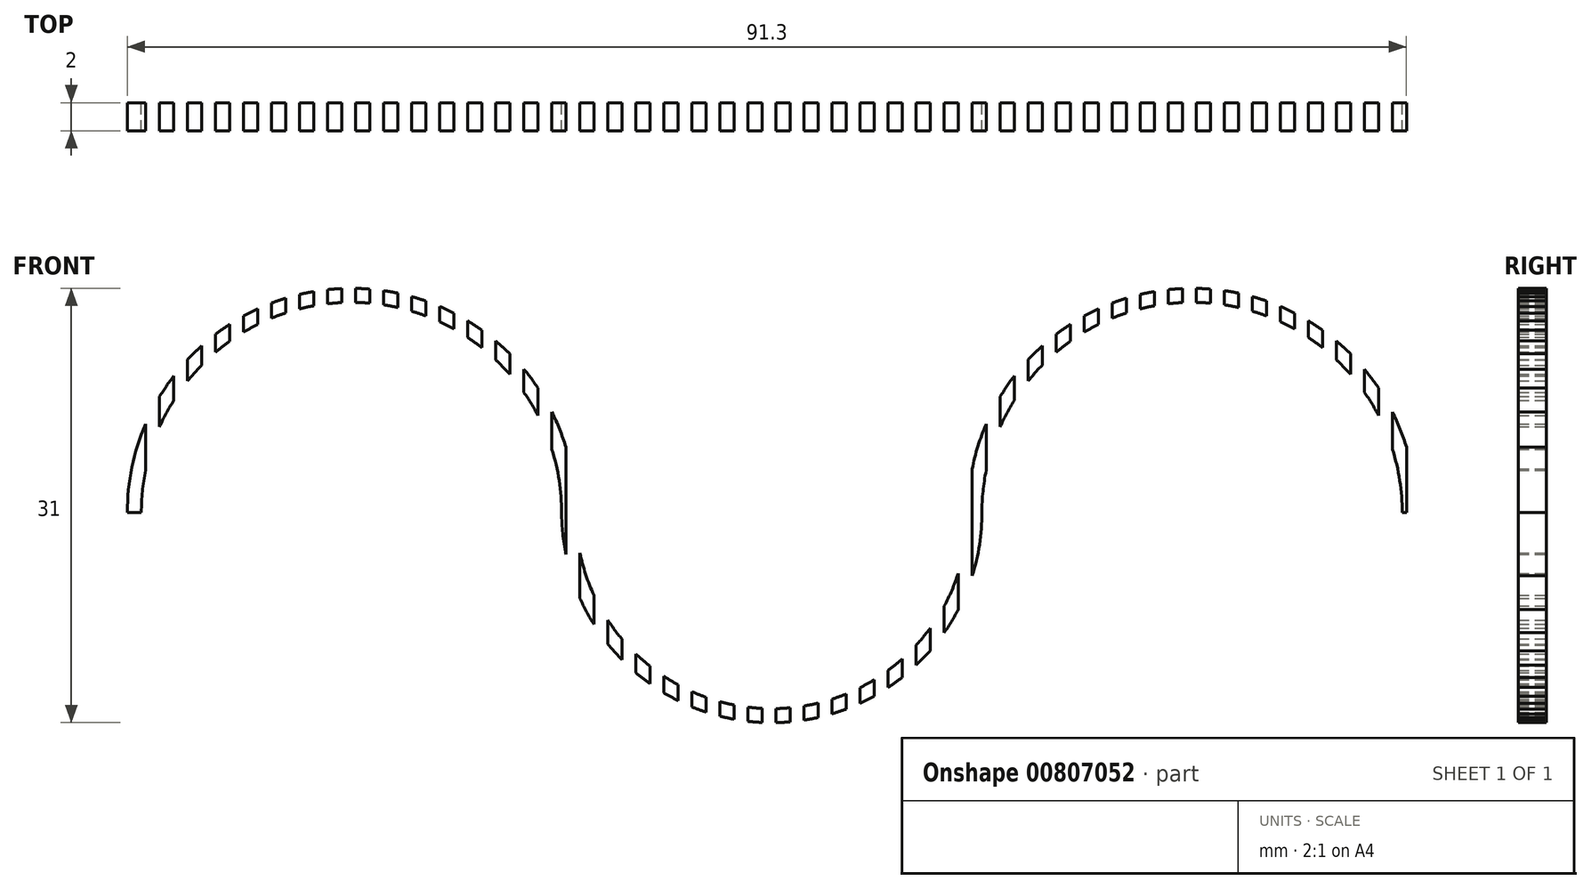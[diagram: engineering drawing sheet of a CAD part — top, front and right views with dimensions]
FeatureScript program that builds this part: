
annotation { "Feature Type Name" : "Feature", "Feature Type Description" : "" }
export const myFeature = defineFeature(function(context is Context, id is Id, definition is map)
    precondition{}
    {
        {
            var Q0;
            Q0=qCreatedBy(makeId("Front.planeOp"),FACE);
            var sketch = newSketch(context, id + "F0", { "sketchPlane" : qUnion([Q0])});
            skArc(sketch, "E0", {"start": v(-15, 0) * mm, "mid": v(0, 15) * mm, "end": v(15, 0) * mm});
            skArc(sketch, "E1", {"start": v(-45, 0) * mm, "mid": v(-30, -15) * mm, "end": v(-15, 0) * mm});
            skLineSegment(sketch, "E2", {"start": v(-15, 0) * mm, "end": v(-84.52, 0) * mm, "construction": true});
            skArc(sketch, "E3", {"start": v(-45, 0) * mm, "mid": v(-60, 15) * mm, "end": v(-75, 0) * mm});
            skArc(sketch, "E4.0", {"start": v(-44, 0) * mm, "mid": v(-60, 16) * mm, "end": v(-76, 0) * mm});
            skArc(sketch, "E4.1", {"start": v(-44, 0) * mm, "mid": v(-30, -14) * mm, "end": v(-16, 0) * mm});
            skArc(sketch, "E4.2", {"start": v(-16, 0) * mm, "mid": v(0, 16) * mm, "end": v(16, 0) * mm});
            skLineSegment(sketch, "E5", {"start": v(-76, 0) * mm, "end": v(-75, 0) * mm});
            skLineSegment(sketch, "E6", {"start": v(15, 0) * mm, "end": v(16, 0) * mm});
            skSolve(sketch);
        }
        {
            var Q0;
            Q0 = qSketchRegion(id + "F0", true);
            extrude(context, id + "F1", {"entities" : qUnion([Q0]), "depth" : 2 * mm, "offsetDistance" : 25 * mm});
        }
        {
            var Q0;
            Q0=qCreatedBy(makeId("Front.planeOp"),FACE);
            var sketch = newSketch(context, id + "F2", { "sketchPlane" : qUnion([Q0])});
            skLineSegment(sketch, "E7.bottom", {"start": v(-74.7, 18.01) * mm, "end": v(-73.7, 18.01) * mm});
            skLineSegment(sketch, "E7.top", {"start": v(-74.7, -16.05) * mm, "end": v(-73.7, -16.05) * mm});
            skLineSegment(sketch, "E7.left", {"start": v(-74.7, 18.01) * mm, "end": v(-74.7, -16.05) * mm});
            skLineSegment(sketch, "E7.right", {"start": v(-73.7, 18.01) * mm, "end": v(-73.7, -16.05) * mm});
            skLineSegment(sketch, "E8.1.0.0", {"start": v(-71.7, 18.01) * mm, "end": v(-71.7, -16.05) * mm});
            skLineSegment(sketch, "E8.1.0.1", {"start": v(-72.7, 18.01) * mm, "end": v(-72.7, -16.05) * mm});
            skLineSegment(sketch, "E8.1.0.2", {"start": v(-72.7, -16.05) * mm, "end": v(-71.7, -16.05) * mm});
            skLineSegment(sketch, "E8.1.0.3", {"start": v(-72.7, 18.01) * mm, "end": v(-71.7, 18.01) * mm});
            skLineSegment(sketch, "E8.2.0.0", {"start": v(-69.7, 18.01) * mm, "end": v(-69.7, -16.05) * mm});
            skLineSegment(sketch, "E8.2.0.1", {"start": v(-70.7, 18.01) * mm, "end": v(-70.7, -16.05) * mm});
            skLineSegment(sketch, "E8.2.0.2", {"start": v(-70.7, -16.05) * mm, "end": v(-69.7, -16.05) * mm});
            skLineSegment(sketch, "E8.2.0.3", {"start": v(-70.7, 18.01) * mm, "end": v(-69.7, 18.01) * mm});
            skLineSegment(sketch, "E8.3.0.0", {"start": v(-67.7, 18.01) * mm, "end": v(-67.7, -16.05) * mm});
            skLineSegment(sketch, "E8.3.0.1", {"start": v(-68.7, 18.01) * mm, "end": v(-68.7, -16.05) * mm});
            skLineSegment(sketch, "E8.3.0.2", {"start": v(-68.7, -16.05) * mm, "end": v(-67.7, -16.05) * mm});
            skLineSegment(sketch, "E8.3.0.3", {"start": v(-68.7, 18.01) * mm, "end": v(-67.7, 18.01) * mm});
            skLineSegment(sketch, "E8.4.0.0", {"start": v(-65.7, 18.01) * mm, "end": v(-65.7, -16.05) * mm});
            skLineSegment(sketch, "E8.4.0.1", {"start": v(-66.7, 18.01) * mm, "end": v(-66.7, -16.05) * mm});
            skLineSegment(sketch, "E8.4.0.2", {"start": v(-66.7, -16.05) * mm, "end": v(-65.7, -16.05) * mm});
            skLineSegment(sketch, "E8.4.0.3", {"start": v(-66.7, 18.01) * mm, "end": v(-65.7, 18.01) * mm});
            skLineSegment(sketch, "E8.5.0.0", {"start": v(-63.7, 18.01) * mm, "end": v(-63.7, -16.05) * mm});
            skLineSegment(sketch, "E8.5.0.1", {"start": v(-64.7, 18.01) * mm, "end": v(-64.7, -16.05) * mm});
            skLineSegment(sketch, "E8.5.0.2", {"start": v(-64.7, -16.05) * mm, "end": v(-63.7, -16.05) * mm});
            skLineSegment(sketch, "E8.5.0.3", {"start": v(-64.7, 18.01) * mm, "end": v(-63.7, 18.01) * mm});
            skLineSegment(sketch, "E8.6.0.0", {"start": v(-61.7, 18.01) * mm, "end": v(-61.7, -16.05) * mm});
            skLineSegment(sketch, "E8.6.0.1", {"start": v(-62.7, 18.01) * mm, "end": v(-62.7, -16.05) * mm});
            skLineSegment(sketch, "E8.6.0.2", {"start": v(-62.7, -16.05) * mm, "end": v(-61.7, -16.05) * mm});
            skLineSegment(sketch, "E8.6.0.3", {"start": v(-62.7, 18.01) * mm, "end": v(-61.7, 18.01) * mm});
            skLineSegment(sketch, "E8.7.0.0", {"start": v(-59.7, 18.01) * mm, "end": v(-59.7, -16.05) * mm});
            skLineSegment(sketch, "E8.7.0.1", {"start": v(-60.7, 18.01) * mm, "end": v(-60.7, -16.05) * mm});
            skLineSegment(sketch, "E8.7.0.2", {"start": v(-60.7, -16.05) * mm, "end": v(-59.7, -16.05) * mm});
            skLineSegment(sketch, "E8.7.0.3", {"start": v(-60.7, 18.01) * mm, "end": v(-59.7, 18.01) * mm});
            skLineSegment(sketch, "E8.8.0.0", {"start": v(-57.7, 18.01) * mm, "end": v(-57.7, -16.05) * mm});
            skLineSegment(sketch, "E8.8.0.1", {"start": v(-58.7, 18.01) * mm, "end": v(-58.7, -16.05) * mm});
            skLineSegment(sketch, "E8.8.0.2", {"start": v(-58.7, -16.05) * mm, "end": v(-57.7, -16.05) * mm});
            skLineSegment(sketch, "E8.8.0.3", {"start": v(-58.7, 18.01) * mm, "end": v(-57.7, 18.01) * mm});
            skLineSegment(sketch, "E8.9.0.0", {"start": v(-55.7, 18.01) * mm, "end": v(-55.7, -16.05) * mm});
            skLineSegment(sketch, "E8.9.0.1", {"start": v(-56.7, 18.01) * mm, "end": v(-56.7, -16.05) * mm});
            skLineSegment(sketch, "E8.9.0.2", {"start": v(-56.7, -16.05) * mm, "end": v(-55.7, -16.05) * mm});
            skLineSegment(sketch, "E8.9.0.3", {"start": v(-56.7, 18.01) * mm, "end": v(-55.7, 18.01) * mm});
            skLineSegment(sketch, "E8.10.0.0", {"start": v(-53.7, 18.01) * mm, "end": v(-53.7, -16.05) * mm});
            skLineSegment(sketch, "E8.10.0.1", {"start": v(-54.7, 18.01) * mm, "end": v(-54.7, -16.05) * mm});
            skLineSegment(sketch, "E8.10.0.2", {"start": v(-54.7, -16.05) * mm, "end": v(-53.7, -16.05) * mm});
            skLineSegment(sketch, "E8.10.0.3", {"start": v(-54.7, 18.01) * mm, "end": v(-53.7, 18.01) * mm});
            skLineSegment(sketch, "E8.11.0.0", {"start": v(-51.7, 18.01) * mm, "end": v(-51.7, -16.05) * mm});
            skLineSegment(sketch, "E8.11.0.1", {"start": v(-52.7, 18.01) * mm, "end": v(-52.7, -16.05) * mm});
            skLineSegment(sketch, "E8.11.0.2", {"start": v(-52.7, -16.05) * mm, "end": v(-51.7, -16.05) * mm});
            skLineSegment(sketch, "E8.11.0.3", {"start": v(-52.7, 18.01) * mm, "end": v(-51.7, 18.01) * mm});
            skLineSegment(sketch, "E8.12.0.0", {"start": v(-49.7, 18.01) * mm, "end": v(-49.7, -16.05) * mm});
            skLineSegment(sketch, "E8.12.0.1", {"start": v(-50.7, 18.01) * mm, "end": v(-50.7, -16.05) * mm});
            skLineSegment(sketch, "E8.12.0.2", {"start": v(-50.7, -16.05) * mm, "end": v(-49.7, -16.05) * mm});
            skLineSegment(sketch, "E8.12.0.3", {"start": v(-50.7, 18.01) * mm, "end": v(-49.7, 18.01) * mm});
            skLineSegment(sketch, "E8.13.0.0", {"start": v(-47.7, 18.01) * mm, "end": v(-47.7, -16.05) * mm});
            skLineSegment(sketch, "E8.13.0.1", {"start": v(-48.7, 18.01) * mm, "end": v(-48.7, -16.05) * mm});
            skLineSegment(sketch, "E8.13.0.2", {"start": v(-48.7, -16.05) * mm, "end": v(-47.7, -16.05) * mm});
            skLineSegment(sketch, "E8.13.0.3", {"start": v(-48.7, 18.01) * mm, "end": v(-47.7, 18.01) * mm});
            skLineSegment(sketch, "E8.14.0.0", {"start": v(-45.7, 18.01) * mm, "end": v(-45.7, -16.05) * mm});
            skLineSegment(sketch, "E8.14.0.1", {"start": v(-46.7, 18.01) * mm, "end": v(-46.7, -16.05) * mm});
            skLineSegment(sketch, "E8.14.0.2", {"start": v(-46.7, -16.05) * mm, "end": v(-45.7, -16.05) * mm});
            skLineSegment(sketch, "E8.14.0.3", {"start": v(-46.7, 18.01) * mm, "end": v(-45.7, 18.01) * mm});
            skLineSegment(sketch, "E8.15.0.0", {"start": v(-43.7, 18.01) * mm, "end": v(-43.7, -16.05) * mm});
            skLineSegment(sketch, "E8.15.0.1", {"start": v(-44.7, 18.01) * mm, "end": v(-44.7, -16.05) * mm});
            skLineSegment(sketch, "E8.15.0.2", {"start": v(-44.7, -16.05) * mm, "end": v(-43.7, -16.05) * mm});
            skLineSegment(sketch, "E8.15.0.3", {"start": v(-44.7, 18.01) * mm, "end": v(-43.7, 18.01) * mm});
            skLineSegment(sketch, "E8.16.0.0", {"start": v(-41.7, 18.01) * mm, "end": v(-41.7, -16.05) * mm});
            skLineSegment(sketch, "E8.16.0.1", {"start": v(-42.7, 18.01) * mm, "end": v(-42.7, -16.05) * mm});
            skLineSegment(sketch, "E8.16.0.2", {"start": v(-42.7, -16.05) * mm, "end": v(-41.7, -16.05) * mm});
            skLineSegment(sketch, "E8.16.0.3", {"start": v(-42.7, 18.01) * mm, "end": v(-41.7, 18.01) * mm});
            skLineSegment(sketch, "E8.17.0.0", {"start": v(-39.7, 18.01) * mm, "end": v(-39.7, -16.05) * mm});
            skLineSegment(sketch, "E8.17.0.1", {"start": v(-40.7, 18.01) * mm, "end": v(-40.7, -16.05) * mm});
            skLineSegment(sketch, "E8.17.0.2", {"start": v(-40.7, -16.05) * mm, "end": v(-39.7, -16.05) * mm});
            skLineSegment(sketch, "E8.17.0.3", {"start": v(-40.7, 18.01) * mm, "end": v(-39.7, 18.01) * mm});
            skLineSegment(sketch, "E8.18.0.0", {"start": v(-37.7, 18.01) * mm, "end": v(-37.7, -16.05) * mm});
            skLineSegment(sketch, "E8.18.0.1", {"start": v(-38.7, 18.01) * mm, "end": v(-38.7, -16.05) * mm});
            skLineSegment(sketch, "E8.18.0.2", {"start": v(-38.7, -16.05) * mm, "end": v(-37.7, -16.05) * mm});
            skLineSegment(sketch, "E8.18.0.3", {"start": v(-38.7, 18.01) * mm, "end": v(-37.7, 18.01) * mm});
            skLineSegment(sketch, "E8.19.0.0", {"start": v(-35.7, 18.01) * mm, "end": v(-35.7, -16.05) * mm});
            skLineSegment(sketch, "E8.19.0.1", {"start": v(-36.7, 18.01) * mm, "end": v(-36.7, -16.05) * mm});
            skLineSegment(sketch, "E8.19.0.2", {"start": v(-36.7, -16.05) * mm, "end": v(-35.7, -16.05) * mm});
            skLineSegment(sketch, "E8.19.0.3", {"start": v(-36.7, 18.01) * mm, "end": v(-35.7, 18.01) * mm});
            skLineSegment(sketch, "E8.20.0.0", {"start": v(-33.7, 18.01) * mm, "end": v(-33.7, -16.05) * mm});
            skLineSegment(sketch, "E8.20.0.1", {"start": v(-34.7, 18.01) * mm, "end": v(-34.7, -16.05) * mm});
            skLineSegment(sketch, "E8.20.0.2", {"start": v(-34.7, -16.05) * mm, "end": v(-33.7, -16.05) * mm});
            skLineSegment(sketch, "E8.20.0.3", {"start": v(-34.7, 18.01) * mm, "end": v(-33.7, 18.01) * mm});
            skLineSegment(sketch, "E8.21.0.0", {"start": v(-31.7, 18.01) * mm, "end": v(-31.7, -16.05) * mm});
            skLineSegment(sketch, "E8.21.0.1", {"start": v(-32.7, 18.01) * mm, "end": v(-32.7, -16.05) * mm});
            skLineSegment(sketch, "E8.21.0.2", {"start": v(-32.7, -16.05) * mm, "end": v(-31.7, -16.05) * mm});
            skLineSegment(sketch, "E8.21.0.3", {"start": v(-32.7, 18.01) * mm, "end": v(-31.7, 18.01) * mm});
            skLineSegment(sketch, "E8.22.0.0", {"start": v(-29.7, 18.01) * mm, "end": v(-29.7, -16.05) * mm});
            skLineSegment(sketch, "E8.22.0.1", {"start": v(-30.7, 18.01) * mm, "end": v(-30.7, -16.05) * mm});
            skLineSegment(sketch, "E8.22.0.2", {"start": v(-30.7, -16.05) * mm, "end": v(-29.7, -16.05) * mm});
            skLineSegment(sketch, "E8.22.0.3", {"start": v(-30.7, 18.01) * mm, "end": v(-29.7, 18.01) * mm});
            skLineSegment(sketch, "E8.23.0.0", {"start": v(-27.7, 18.01) * mm, "end": v(-27.7, -16.05) * mm});
            skLineSegment(sketch, "E8.23.0.1", {"start": v(-28.7, 18.01) * mm, "end": v(-28.7, -16.05) * mm});
            skLineSegment(sketch, "E8.23.0.2", {"start": v(-28.7, -16.05) * mm, "end": v(-27.7, -16.05) * mm});
            skLineSegment(sketch, "E8.23.0.3", {"start": v(-28.7, 18.01) * mm, "end": v(-27.7, 18.01) * mm});
            skLineSegment(sketch, "E8.24.0.0", {"start": v(-25.7, 18.01) * mm, "end": v(-25.7, -16.05) * mm});
            skLineSegment(sketch, "E8.24.0.1", {"start": v(-26.7, 18.01) * mm, "end": v(-26.7, -16.05) * mm});
            skLineSegment(sketch, "E8.24.0.2", {"start": v(-26.7, -16.05) * mm, "end": v(-25.7, -16.05) * mm});
            skLineSegment(sketch, "E8.24.0.3", {"start": v(-26.7, 18.01) * mm, "end": v(-25.7, 18.01) * mm});
            skLineSegment(sketch, "E8.25.0.0", {"start": v(-23.7, 18.01) * mm, "end": v(-23.7, -16.05) * mm});
            skLineSegment(sketch, "E8.25.0.1", {"start": v(-24.7, 18.01) * mm, "end": v(-24.7, -16.05) * mm});
            skLineSegment(sketch, "E8.25.0.2", {"start": v(-24.7, -16.05) * mm, "end": v(-23.7, -16.05) * mm});
            skLineSegment(sketch, "E8.25.0.3", {"start": v(-24.7, 18.01) * mm, "end": v(-23.7, 18.01) * mm});
            skLineSegment(sketch, "E8.26.0.0", {"start": v(-21.7, 18.01) * mm, "end": v(-21.7, -16.05) * mm});
            skLineSegment(sketch, "E8.26.0.1", {"start": v(-22.7, 18.01) * mm, "end": v(-22.7, -16.05) * mm});
            skLineSegment(sketch, "E8.26.0.2", {"start": v(-22.7, -16.05) * mm, "end": v(-21.7, -16.05) * mm});
            skLineSegment(sketch, "E8.26.0.3", {"start": v(-22.7, 18.01) * mm, "end": v(-21.7, 18.01) * mm});
            skLineSegment(sketch, "E8.27.0.0", {"start": v(-19.7, 18.01) * mm, "end": v(-19.7, -16.05) * mm});
            skLineSegment(sketch, "E8.27.0.1", {"start": v(-20.7, 18.01) * mm, "end": v(-20.7, -16.05) * mm});
            skLineSegment(sketch, "E8.27.0.2", {"start": v(-20.7, -16.05) * mm, "end": v(-19.7, -16.05) * mm});
            skLineSegment(sketch, "E8.27.0.3", {"start": v(-20.7, 18.01) * mm, "end": v(-19.7, 18.01) * mm});
            skLineSegment(sketch, "E8.28.0.0", {"start": v(-17.7, 18.01) * mm, "end": v(-17.7, -16.05) * mm});
            skLineSegment(sketch, "E8.28.0.1", {"start": v(-18.7, 18.01) * mm, "end": v(-18.7, -16.05) * mm});
            skLineSegment(sketch, "E8.28.0.2", {"start": v(-18.7, -16.05) * mm, "end": v(-17.7, -16.05) * mm});
            skLineSegment(sketch, "E8.28.0.3", {"start": v(-18.7, 18.01) * mm, "end": v(-17.7, 18.01) * mm});
            skLineSegment(sketch, "E8.29.0.0", {"start": v(-15.7, 18.01) * mm, "end": v(-15.7, -16.05) * mm});
            skLineSegment(sketch, "E8.29.0.1", {"start": v(-16.7, 18.01) * mm, "end": v(-16.7, -16.05) * mm});
            skLineSegment(sketch, "E8.29.0.2", {"start": v(-16.7, -16.05) * mm, "end": v(-15.7, -16.05) * mm});
            skLineSegment(sketch, "E8.29.0.3", {"start": v(-16.7, 18.01) * mm, "end": v(-15.7, 18.01) * mm});
            skLineSegment(sketch, "E8.30.0.0", {"start": v(-13.7, 18.01) * mm, "end": v(-13.7, -16.05) * mm});
            skLineSegment(sketch, "E8.30.0.1", {"start": v(-14.7, 18.01) * mm, "end": v(-14.7, -16.05) * mm});
            skLineSegment(sketch, "E8.30.0.2", {"start": v(-14.7, -16.05) * mm, "end": v(-13.7, -16.05) * mm});
            skLineSegment(sketch, "E8.30.0.3", {"start": v(-14.7, 18.01) * mm, "end": v(-13.7, 18.01) * mm});
            skLineSegment(sketch, "E8.31.0.0", {"start": v(-11.7, 18.01) * mm, "end": v(-11.7, -16.05) * mm});
            skLineSegment(sketch, "E8.31.0.1", {"start": v(-12.7, 18.01) * mm, "end": v(-12.7, -16.05) * mm});
            skLineSegment(sketch, "E8.31.0.2", {"start": v(-12.7, -16.05) * mm, "end": v(-11.7, -16.05) * mm});
            skLineSegment(sketch, "E8.31.0.3", {"start": v(-12.7, 18.01) * mm, "end": v(-11.7, 18.01) * mm});
            skLineSegment(sketch, "E8.32.0.0", {"start": v(-9.7, 18.01) * mm, "end": v(-9.7, -16.05) * mm});
            skLineSegment(sketch, "E8.32.0.1", {"start": v(-10.7, 18.01) * mm, "end": v(-10.7, -16.05) * mm});
            skLineSegment(sketch, "E8.32.0.2", {"start": v(-10.7, -16.05) * mm, "end": v(-9.7, -16.05) * mm});
            skLineSegment(sketch, "E8.32.0.3", {"start": v(-10.7, 18.01) * mm, "end": v(-9.7, 18.01) * mm});
            skLineSegment(sketch, "E8.33.0.0", {"start": v(-7.7, 18.01) * mm, "end": v(-7.7, -16.05) * mm});
            skLineSegment(sketch, "E8.33.0.1", {"start": v(-8.7, 18.01) * mm, "end": v(-8.7, -16.05) * mm});
            skLineSegment(sketch, "E8.33.0.2", {"start": v(-8.7, -16.05) * mm, "end": v(-7.7, -16.05) * mm});
            skLineSegment(sketch, "E8.33.0.3", {"start": v(-8.7, 18.01) * mm, "end": v(-7.7, 18.01) * mm});
            skLineSegment(sketch, "E8.34.0.0", {"start": v(-5.7, 18.01) * mm, "end": v(-5.7, -16.05) * mm});
            skLineSegment(sketch, "E8.34.0.1", {"start": v(-6.7, 18.01) * mm, "end": v(-6.7, -16.05) * mm});
            skLineSegment(sketch, "E8.34.0.2", {"start": v(-6.7, -16.05) * mm, "end": v(-5.7, -16.05) * mm});
            skLineSegment(sketch, "E8.34.0.3", {"start": v(-6.7, 18.01) * mm, "end": v(-5.7, 18.01) * mm});
            skLineSegment(sketch, "E8.35.0.0", {"start": v(-3.7, 18.01) * mm, "end": v(-3.7, -16.05) * mm});
            skLineSegment(sketch, "E8.35.0.1", {"start": v(-4.7, 18.01) * mm, "end": v(-4.7, -16.05) * mm});
            skLineSegment(sketch, "E8.35.0.2", {"start": v(-4.7, -16.05) * mm, "end": v(-3.7, -16.05) * mm});
            skLineSegment(sketch, "E8.35.0.3", {"start": v(-4.7, 18.01) * mm, "end": v(-3.7, 18.01) * mm});
            skLineSegment(sketch, "E8.36.0.0", {"start": v(-1.7, 18.01) * mm, "end": v(-1.7, -16.05) * mm});
            skLineSegment(sketch, "E8.36.0.1", {"start": v(-2.7, 18.01) * mm, "end": v(-2.7, -16.05) * mm});
            skLineSegment(sketch, "E8.36.0.2", {"start": v(-2.7, -16.05) * mm, "end": v(-1.7, -16.05) * mm});
            skLineSegment(sketch, "E8.36.0.3", {"start": v(-2.7, 18.01) * mm, "end": v(-1.7, 18.01) * mm});
            skLineSegment(sketch, "E8.37.0.0", {"start": v(0.3, 18.01) * mm, "end": v(0.3, -16.05) * mm});
            skLineSegment(sketch, "E8.37.0.1", {"start": v(-0.7, 18.01) * mm, "end": v(-0.7, -16.05) * mm});
            skLineSegment(sketch, "E8.37.0.2", {"start": v(-0.7, -16.05) * mm, "end": v(0.3, -16.05) * mm});
            skLineSegment(sketch, "E8.37.0.3", {"start": v(-0.7, 18.01) * mm, "end": v(0.3, 18.01) * mm});
            skLineSegment(sketch, "E8.38.0.0", {"start": v(2.3, 18.01) * mm, "end": v(2.3, -16.05) * mm});
            skLineSegment(sketch, "E8.38.0.1", {"start": v(1.3, 18.01) * mm, "end": v(1.3, -16.05) * mm});
            skLineSegment(sketch, "E8.38.0.2", {"start": v(1.3, -16.05) * mm, "end": v(2.3, -16.05) * mm});
            skLineSegment(sketch, "E8.38.0.3", {"start": v(1.3, 18.01) * mm, "end": v(2.3, 18.01) * mm});
            skLineSegment(sketch, "E8.39.0.0", {"start": v(4.3, 18.01) * mm, "end": v(4.3, -16.05) * mm});
            skLineSegment(sketch, "E8.39.0.1", {"start": v(3.3, 18.01) * mm, "end": v(3.3, -16.05) * mm});
            skLineSegment(sketch, "E8.39.0.2", {"start": v(3.3, -16.05) * mm, "end": v(4.3, -16.05) * mm});
            skLineSegment(sketch, "E8.39.0.3", {"start": v(3.3, 18.01) * mm, "end": v(4.3, 18.01) * mm});
            skLineSegment(sketch, "E8.40.0.0", {"start": v(6.3, 18.01) * mm, "end": v(6.3, -16.05) * mm});
            skLineSegment(sketch, "E8.40.0.1", {"start": v(5.3, 18.01) * mm, "end": v(5.3, -16.05) * mm});
            skLineSegment(sketch, "E8.40.0.2", {"start": v(5.3, -16.05) * mm, "end": v(6.3, -16.05) * mm});
            skLineSegment(sketch, "E8.40.0.3", {"start": v(5.3, 18.01) * mm, "end": v(6.3, 18.01) * mm});
            skLineSegment(sketch, "E8.41.0.0", {"start": v(8.3, 18.01) * mm, "end": v(8.3, -16.05) * mm});
            skLineSegment(sketch, "E8.41.0.1", {"start": v(7.3, 18.01) * mm, "end": v(7.3, -16.05) * mm});
            skLineSegment(sketch, "E8.41.0.2", {"start": v(7.3, -16.05) * mm, "end": v(8.3, -16.05) * mm});
            skLineSegment(sketch, "E8.41.0.3", {"start": v(7.3, 18.01) * mm, "end": v(8.3, 18.01) * mm});
            skLineSegment(sketch, "E8.42.0.0", {"start": v(10.3, 18.01) * mm, "end": v(10.3, -16.05) * mm});
            skLineSegment(sketch, "E8.42.0.1", {"start": v(9.3, 18.01) * mm, "end": v(9.3, -16.05) * mm});
            skLineSegment(sketch, "E8.42.0.2", {"start": v(9.3, -16.05) * mm, "end": v(10.3, -16.05) * mm});
            skLineSegment(sketch, "E8.42.0.3", {"start": v(9.3, 18.01) * mm, "end": v(10.3, 18.01) * mm});
            skLineSegment(sketch, "E8.43.0.0", {"start": v(12.3, 18.01) * mm, "end": v(12.3, -16.05) * mm});
            skLineSegment(sketch, "E8.43.0.1", {"start": v(11.3, 18.01) * mm, "end": v(11.3, -16.05) * mm});
            skLineSegment(sketch, "E8.43.0.2", {"start": v(11.3, -16.05) * mm, "end": v(12.3, -16.05) * mm});
            skLineSegment(sketch, "E8.43.0.3", {"start": v(11.3, 18.01) * mm, "end": v(12.3, 18.01) * mm});
            skLineSegment(sketch, "E8.44.0.0", {"start": v(14.3, 18.01) * mm, "end": v(14.3, -16.05) * mm});
            skLineSegment(sketch, "E8.44.0.1", {"start": v(13.3, 18.01) * mm, "end": v(13.3, -16.05) * mm});
            skLineSegment(sketch, "E8.44.0.2", {"start": v(13.3, -16.05) * mm, "end": v(14.3, -16.05) * mm});
            skLineSegment(sketch, "E8.44.0.3", {"start": v(13.3, 18.01) * mm, "end": v(14.3, 18.01) * mm});
            skLineSegment(sketch, "E8.45.0.0", {"start": v(16.3, 18.01) * mm, "end": v(16.3, -16.05) * mm});
            skLineSegment(sketch, "E8.45.0.1", {"start": v(15.3, 18.01) * mm, "end": v(15.3, -16.05) * mm});
            skLineSegment(sketch, "E8.45.0.2", {"start": v(15.3, -16.05) * mm, "end": v(16.3, -16.05) * mm});
            skLineSegment(sketch, "E8.45.0.3", {"start": v(15.3, 18.01) * mm, "end": v(16.3, 18.01) * mm});
            skLineSegment(sketch, "E8.direction1", {"start": v(-74.7, -16.05) * mm, "end": v(-72.7, -16.05) * mm, "construction": true});
            skSolve(sketch);
        }
        {
            var Q0;
            Q0 = qSketchRegion(id + "F2", true);
            extrude(context, id + "F3", {"entities" : qUnion([Q0]), "operationType" : NewBodyOperationType.REMOVE, "depth" : 25 * mm, "offsetDistance" : 25 * mm});
        }
    });
